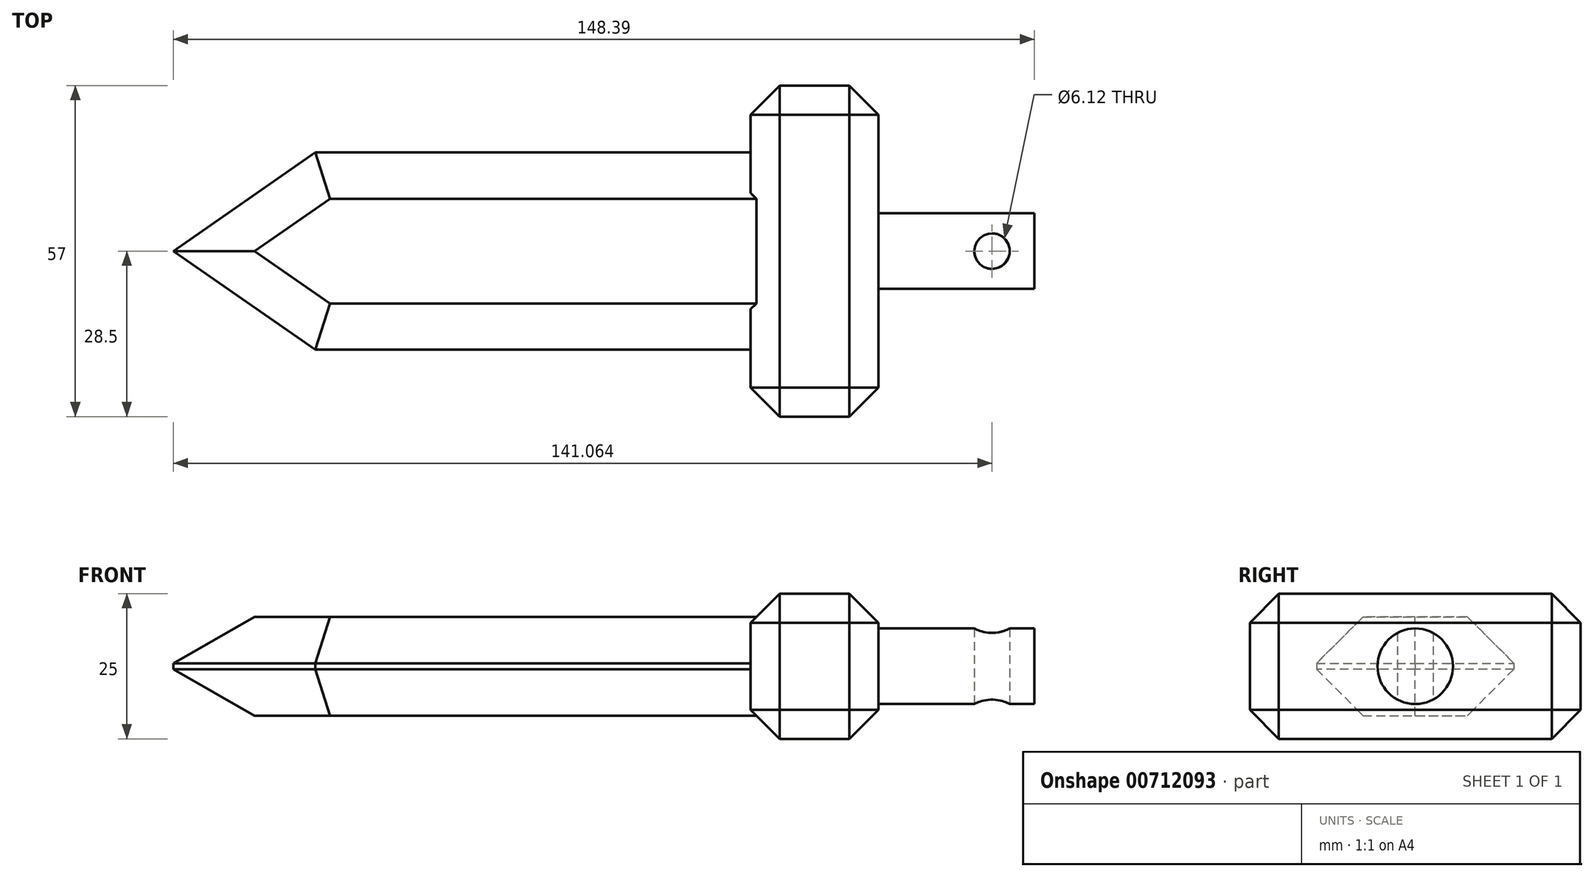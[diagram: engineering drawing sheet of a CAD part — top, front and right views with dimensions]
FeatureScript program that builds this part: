
annotation { "Feature Type Name" : "Feature", "Feature Type Description" : "" }
export const myFeature = defineFeature(function(context is Context, id is Id, definition is map)
    precondition{}
    {
        {
            var Q0;
            Q0=qCreatedBy(makeId("Top.planeOp"),FACE);
            var sketch = newSketch(context, id + "F0", { "sketchPlane" : qUnion([Q0])});
            skLineSegment(sketch, "E0.bottom", {"start": v(47.03, -28.5) * mm, "end": v(25.03, -28.5) * mm});
            skLineSegment(sketch, "E0.top", {"start": v(47.03, 28.5) * mm, "end": v(25.03, 28.5) * mm});
            skLineSegment(sketch, "E0.left", {"start": v(47.03, -28.5) * mm, "end": v(47.03, 0) * mm});
            skLineSegment(sketch, "E0.right", {"start": v(25.03, -28.5) * mm, "end": v(25.03, 28.5) * mm});
            skPoint(sketch, "E0.middle", {"position": v(36.03, 0) * mm});
            skLineSegment(sketch, "E1.bottom", {"start": v(25.03, -17) * mm, "end": v(-49.97, -17) * mm});
            skLineSegment(sketch, "E1.top", {"start": v(25.03, 17) * mm, "end": v(-49.97, 17) * mm});
            skLineSegment(sketch, "E1.left", {"start": v(25.03, -17) * mm, "end": v(25.03, 17) * mm});
            skPoint(sketch, "E1.middle", {"position": v(-12.47, 0) * mm});
            skLineSegment(sketch, "E2", {"start": v(-74.46, 0) * mm, "end": v(-49.97, -17) * mm});
            skLineSegment(sketch, "E3", {"start": v(-74.46, 0) * mm, "end": v(-49.97, 17) * mm});
            skLineSegment(sketch, "E4", {"start": v(47.03, 0) * mm, "end": v(47.03, 28.5) * mm});
            skSolve(sketch);
        }
        {
            var Q0;
            {var subQ1=sQuery(id+"F0.wireOp",EDGE,"E0.bottom");Q0=makeQuery(id+"F0.imprint","IMPRINT",FACE,{"disambiguationData":[TD([[makeQuery(id+"F0.imprint","IMPRINT",EDGE,{"derivedFrom":subQ1}),-1.0]])]});}
            extrude(context, id + "F1", {"entities" : qUnion([Q0]), "endBound" : BoundingType.SYMMETRIC, "oppositeDirection" : true, "depth" : 25 * mm, "offsetDistance" : 25 * mm});
        }
        {
            var Q0;
            Q0=makeQuery(id+"F0.imprint","IMPRINT",FACE,{"disambiguationData":[TD([[makeQuery(id+"F0.imprint","IMPRINT",EDGE,{"derivedFrom":sQuery(id+"F0.wireOp",EDGE,"E1.bottom")}),-1.0]])]});
            extrude(context, id + "F2", {"entities" : qUnion([Q0]), "operationType" : NewBodyOperationType.ADD, "endBound" : BoundingType.SYMMETRIC, "depth" : 17 * mm, "offsetDistance" : 25 * mm});
        }
        {
            var Q0;
            Q0=makeQuery(id+"F2.opExtrude","CAP_EDGE",EDGE,{"disambiguationData":[OSD([sQuery(id+"F0.wireOp",EDGE,"E1.top")])],"isStart":true});
            var Q1;
            Q1=makeQuery(id+"F2.opExtrude","CAP_EDGE",EDGE,{"disambiguationData":[OSD([sQuery(id+"F0.wireOp",EDGE,"E1.bottom")])],"isStart":true});
            var Q2;
            Q2=makeQuery(id+"F2.opExtrude","CAP_EDGE",EDGE,{"disambiguationData":[OSD([sQuery(id+"F0.wireOp",EDGE,"E2")])],"isStart":true});
            var Q3;
            Q3=makeQuery(id+"F2.opExtrude","CAP_EDGE",EDGE,{"disambiguationData":[OSD([sQuery(id+"F0.wireOp",EDGE,"E1.bottom")])],"isStart":false});
            var Q4;
            Q4=makeQuery(id+"F2.opExtrude","CAP_EDGE",EDGE,{"disambiguationData":[OSD([sQuery(id+"F0.wireOp",EDGE,"E1.top")])],"isStart":false});
            var Q5;
            Q5=makeQuery(id+"F2.opExtrude","CAP_EDGE",EDGE,{"disambiguationData":[OSD([sQuery(id+"F0.wireOp",EDGE,"E2")])],"isStart":false});
            var Q6;
            Q6=makeQuery(id+"F2.opExtrude","CAP_EDGE",EDGE,{"disambiguationData":[OSD([sQuery(id+"F0.wireOp",EDGE,"E3")])],"isStart":false});
            var Q7;
            Q7=makeQuery(id+"F2.opExtrude","CAP_EDGE",EDGE,{"disambiguationData":[OSD([sQuery(id+"F0.wireOp",EDGE,"E3")])],"isStart":true});
            chamfer(context, id + "F3", {"entities" : qUnion([Q0, Q1, Q2, Q3, Q4, Q5, Q6, Q7]), "width" : 8 * mm, "tangentPropagation" : true});
        }
        {
            var Q0;
            Q0=makeQuery(id+"F1.opExtrude","CAP_EDGE",EDGE,{"disambiguationData":[OSD([sQuery(id+"F0.wireOp",EDGE,"E0.right"),sQuery(id+"F0.wireOp",EDGE,"E1.left")])],"isStart":false});
            var Q1;
            Q1=makeQuery(id+"F1.opExtrude","SWEPT_EDGE",EDGE,{"disambiguationData":[OSD([sQuery(id+"F0.wireOp",EDGE,"E0.bottom"),sQuery(id+"F0.wireOp",EDGE,"E0.right")])]});
            var Q2;
            Q2=makeQuery(id+"F1.opExtrude","CAP_EDGE",EDGE,{"disambiguationData":[OSD([sQuery(id+"F0.wireOp",EDGE,"E0.right"),sQuery(id+"F0.wireOp",EDGE,"E1.left")])],"isStart":true});
            var Q3;
            Q3=makeQuery(id+"F1.opExtrude","SWEPT_EDGE",EDGE,{"disambiguationData":[OSD([sQuery(id+"F0.wireOp",EDGE,"E0.top"),sQuery(id+"F0.wireOp",EDGE,"E0.right")])]});
            var Q4;
            Q4=makeQuery(id+"F1.opExtrude","CAP_EDGE",EDGE,{"disambiguationData":[OSD([sQuery(id+"F0.wireOp",EDGE,"E0.top")])],"isStart":false});
            var Q5;
            Q5=makeQuery(id+"F1.opExtrude","CAP_EDGE",EDGE,{"disambiguationData":[OSD([sQuery(id+"F0.wireOp",EDGE,"E0.top")])],"isStart":true});
            var Q6;
            Q6=makeQuery(id+"F1.opExtrude","SWEPT_EDGE",EDGE,{"disambiguationData":[OSD([sQuery(id+"F0.wireOp",EDGE,"E0.top"),sQuery(id+"F0.wireOp",EDGE,"E4")])]});
            var Q7;
            Q7=makeQuery(id+"F1.opExtrude","CAP_EDGE",EDGE,{"disambiguationData":[OSD([sQuery(id+"F0.wireOp",EDGE,"E0.bottom")])],"isStart":false});
            var Q8;
            Q8=makeQuery(id+"F1.opExtrude","CAP_EDGE",EDGE,{"disambiguationData":[OSD([sQuery(id+"F0.wireOp",EDGE,"E0.bottom")])],"isStart":true});
            var Q9;
            Q9=makeQuery(id+"F1.opExtrude","CAP_EDGE",EDGE,{"disambiguationData":[OSD([sQuery(id+"F0.wireOp",EDGE,"E0.left"),sQuery(id+"F0.wireOp",EDGE,"E4")])],"isStart":true});
            var Q10;
            Q10=makeQuery(id+"F1.opExtrude","CAP_EDGE",EDGE,{"disambiguationData":[OSD([sQuery(id+"F0.wireOp",EDGE,"E0.left"),sQuery(id+"F0.wireOp",EDGE,"E4")])],"isStart":false});
            var Q11;
            Q11=makeQuery(id+"F1.opExtrude","SWEPT_EDGE",EDGE,{"disambiguationData":[OSD([sQuery(id+"F0.wireOp",EDGE,"E0.bottom"),sQuery(id+"F0.wireOp",EDGE,"E0.left")])]});
            chamfer(context, id + "F4", {"entities" : qUnion([Q0, Q1, Q2, Q3, Q4, Q5, Q6, Q7, Q8, Q9, Q10, Q11]), "width" : 5 * mm, "tangentPropagation" : true});
        }
        {
            var Q0;
            Q0=makeQuery(id+"F1.opExtrude","SWEPT_FACE",FACE,{"disambiguationData":[OSD([sQuery(id+"F0.wireOp",EDGE,"E0.left"),sQuery(id+"F0.wireOp",EDGE,"E4")])]});
            var sketch = newSketch(context, id + "F5", { "sketchPlane" : qUnion([Q0])});
            skCircle(sketch, "E5", {"center": v(0, 0) * mm, "radius": 6.5 * mm});
            skSolve(sketch);
        }
        {
            var Q0;
            Q0=makeQuery(id+"F5.imprint","IMPRINT",FACE,{"disambiguationData":[TD([[makeQuery(id+"F5.imprint","IMPRINT",EDGE,{"derivedFrom":sQuery(id+"F5.wireOp",EDGE,"E5")}),1.0]])]});
            extrude(context, id + "F6", {"entities" : qUnion([Q0]), "operationType" : NewBodyOperationType.ADD, "depth" : 26.9 * mm, "offsetDistance" : 25 * mm});
        }
        {
            var Q0;
            Q0=qCreatedBy(makeId("Top.planeOp"),FACE);
            var sketch = newSketch(context, id + "F7", { "sketchPlane" : qUnion([Q0])});
            skPoint(sketch, "E6", {"position": v(66.6, 0) * mm});
            skCircle(sketch, "E7", {"center": v(66.6, 0) * mm, "radius": 3.06 * mm});
            skSolve(sketch);
        }
        {
            var Q0;
            Q0=makeQuery(id+"F7.imprint","IMPRINT",FACE,{"disambiguationData":[TD([[makeQuery(id+"F7.imprint","IMPRINT",EDGE,{"derivedFrom":sQuery(id+"F7.wireOp",EDGE,"E7")}),1.0]])]});
            var Q1;
            Q1=sQuery(id+"F7.wireOp",EDGE,"E7");
            extrude(context, id + "F8", {"entities" : qUnion([Q0]), "operationType" : NewBodyOperationType.REMOVE, "surfaceEntities" : qUnion([Q1]), "endBound" : BoundingType.SYMMETRIC, "depth" : 13 * mm, "offsetDistance" : 25 * mm});
        }
    });
